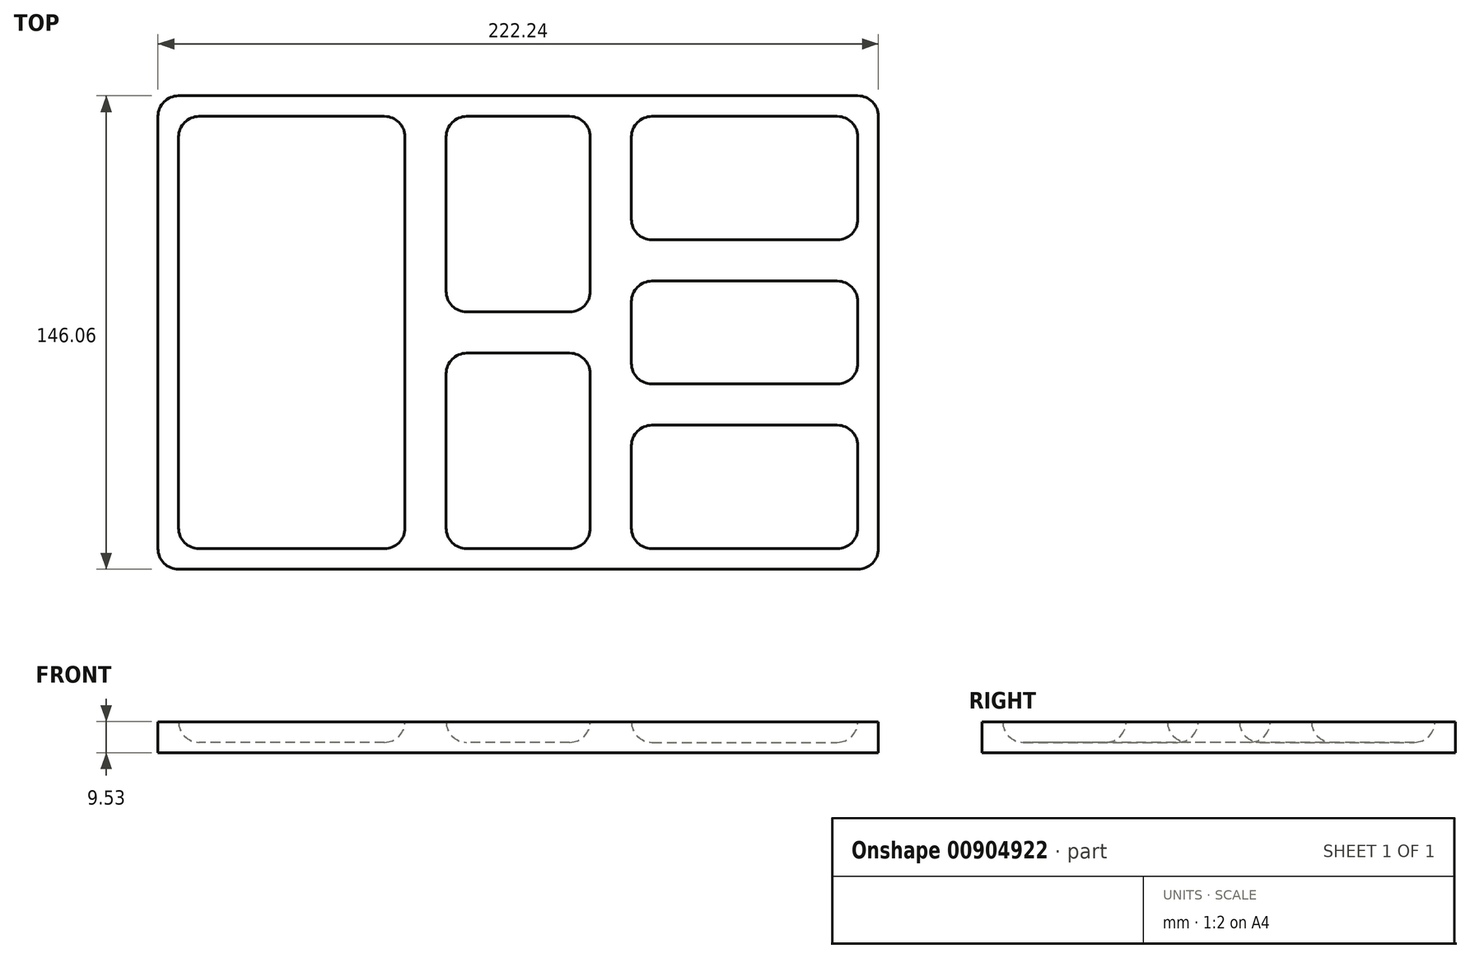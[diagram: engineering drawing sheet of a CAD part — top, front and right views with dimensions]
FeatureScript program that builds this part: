
annotation { "Feature Type Name" : "Feature", "Feature Type Description" : "" }
export const myFeature = defineFeature(function(context is Context, id is Id, definition is map)
    precondition{}
    {
        {
            var Q0;
            Q0=qCreatedBy(makeId("Top.planeOp"),FACE);
            var sketch = newSketch(context, id + "F0", { "sketchPlane" : qUnion([Q0])});
            skLineSegment(sketch, "E0.bottom", {"start": v(111.12, 73.03) * mm, "end": v(-111.13, 73.03) * mm});
            skLineSegment(sketch, "E0.top", {"start": v(111.13, -73.03) * mm, "end": v(-111.12, -73.03) * mm});
            skLineSegment(sketch, "E0.left", {"start": v(111.12, 73.03) * mm, "end": v(111.13, -73.03) * mm});
            skLineSegment(sketch, "E0.right", {"start": v(-111.13, 73.03) * mm, "end": v(-111.12, -73.03) * mm});
            skPoint(sketch, "E0.middle", {"position": v(0, 0) * mm});
            skSolve(sketch);
        }
        {
            var Q0;
            Q0 = qSketchRegion(id + "F0", true);
            extrude(context, id + "F1", {"entities" : qUnion([Q0]), "depth" : 9.52 * mm, "offsetDistance" : 25.4 * mm});
        }
        {
            var Q0;
            Q0=makeQuery(id+"F1.opExtrude","CAP_FACE",FACE,{"disambiguationData":[OSD([sQuery(id+"F0.wireOp",EDGE,"E0.bottom"),sQuery(id+"F0.wireOp",EDGE,"E0.top"),sQuery(id+"F0.wireOp",EDGE,"E0.left"),sQuery(id+"F0.wireOp",EDGE,"E0.right")])],"isStart":false});
            var sketch = newSketch(context, id + "F2", { "sketchPlane" : qUnion([Q0])});
            skLineSegment(sketch, "E1.bottom", {"start": v(104.78, 66.68) * mm, "end": v(34.93, 66.68) * mm});
            skLineSegment(sketch, "E1.top", {"start": v(104.78, -66.68) * mm, "end": v(34.93, -66.68) * mm});
            skLineSegment(sketch, "E1.left", {"start": v(104.78, 66.68) * mm, "end": v(104.78, 28.58) * mm});
            skLineSegment(sketch, "E1.right", {"start": v(-104.78, 66.68) * mm, "end": v(-104.78, -66.68) * mm});
            skPoint(sketch, "E1.middle", {"position": v(0, 0) * mm});
            skLineSegment(sketch, "E2", {"start": v(-104.78, 22.23) * mm, "end": v(104.78, 22.23) * mm, "construction": true});
            skLineSegment(sketch, "E3", {"start": v(-104.78, -22.23) * mm, "end": v(104.78, -22.23) * mm, "construction": true});
            skLineSegment(sketch, "E4", {"start": v(28.57, 66.68) * mm, "end": v(28.58, -66.68) * mm, "construction": true});
            skLineSegment(sketch, "E5", {"start": v(34.92, 66.68) * mm, "end": v(34.92, 28.57) * mm});
            skLineSegment(sketch, "E6", {"start": v(34.92, 28.57) * mm, "end": v(104.78, 28.58) * mm});
            skLineSegment(sketch, "E7", {"start": v(104.78, 15.88) * mm, "end": v(34.93, 15.87) * mm});
            skLineSegment(sketch, "E8", {"start": v(34.93, 15.87) * mm, "end": v(34.93, -15.88) * mm});
            skLineSegment(sketch, "E9", {"start": v(34.93, -15.88) * mm, "end": v(104.78, -15.88) * mm});
            skLineSegment(sketch, "E10", {"start": v(104.78, -28.58) * mm, "end": v(34.93, -28.58) * mm});
            skLineSegment(sketch, "E11", {"start": v(34.93, -28.58) * mm, "end": v(34.93, -66.68) * mm});
            skLineSegment(sketch, "E12", {"start": v(22.23, -66.68) * mm, "end": v(22.23, -6.35) * mm});
            skLineSegment(sketch, "E13.trimOffspring", {"start": v(22.23, 66.68) * mm, "end": v(-22.22, 66.68) * mm});
            skLineSegment(sketch, "E14.trimOffspring", {"start": v(104.78, 15.88) * mm, "end": v(104.78, -15.88) * mm});
            skLineSegment(sketch, "E15.trimOffspring", {"start": v(104.78, -28.58) * mm, "end": v(104.78, -66.68) * mm});
            skLineSegment(sketch, "E16.trimOffspring", {"start": v(22.23, -66.68) * mm, "end": v(-22.22, -66.68) * mm});
            skLineSegment(sketch, "E17", {"start": v(-28.58, 66.68) * mm, "end": v(-28.57, -66.68) * mm, "construction": true});
            skLineSegment(sketch, "E18", {"start": v(22.23, 0) * mm, "end": v(-28.58, 0) * mm, "construction": true});
            skLineSegment(sketch, "E19", {"start": v(-34.93, 66.68) * mm, "end": v(-34.92, -66.68) * mm});
            skLineSegment(sketch, "E20", {"start": v(-22.22, -66.68) * mm, "end": v(-22.23, -6.35) * mm});
            skLineSegment(sketch, "E21", {"start": v(-22.23, -6.35) * mm, "end": v(22.23, -6.35) * mm});
            skLineSegment(sketch, "E22", {"start": v(22.23, 6.35) * mm, "end": v(-22.22, 6.35) * mm});
            skLineSegment(sketch, "E23", {"start": v(-22.22, 6.35) * mm, "end": v(-22.23, 66.68) * mm});
            skLineSegment(sketch, "E24.trimOffspring", {"start": v(-34.92, 66.68) * mm, "end": v(-104.78, 66.68) * mm});
            skLineSegment(sketch, "E25.trimOffspring", {"start": v(-34.92, -66.68) * mm, "end": v(-104.78, -66.68) * mm});
            skLineSegment(sketch, "E26.trimOffspring", {"start": v(22.23, 6.35) * mm, "end": v(22.22, 66.68) * mm});
            skSolve(sketch);
        }
        {
            var Q0;
            Q0 = qSketchRegion(id + "F2", true);
            extrude(context, id + "F3", {"entities" : qUnion([Q0]), "operationType" : NewBodyOperationType.REMOVE, "oppositeDirection" : true, "depth" : 6.35 * mm, "offsetDistance" : 25.4 * mm});
        }
        {
            var Q0;
            Q0=makeQuery(id+"F3.boolean.opBoolean","COPY",EDGE,{"derivedFrom":makeQuery(id+"F3.opExtrude","SWEPT_EDGE",EDGE,{"disambiguationData":[OSD([sQuery(id+"F2.wireOp",EDGE,"E1.right"),sQuery(id+"F2.wireOp",EDGE,"E13.trimOffspring")])]})});
            var Q1;
            Q1=makeQuery(id+"F3.boolean.opBoolean","COPY",EDGE,{"derivedFrom":makeQuery(id+"F3.opExtrude","SWEPT_EDGE",EDGE,{"disambiguationData":[OSD([sQuery(id+"F2.wireOp",EDGE,"E12"),sQuery(id+"F2.wireOp",EDGE,"E13.trimOffspring")])]})});
            var Q2;
            Q2=makeQuery(id+"F3.boolean.opBoolean","COPY",EDGE,{"derivedFrom":makeQuery(id+"F3.opExtrude","SWEPT_EDGE",EDGE,{"disambiguationData":[OSD([sQuery(id+"F2.wireOp",EDGE,"E1.right"),sQuery(id+"F2.wireOp",EDGE,"E16.trimOffspring")])]})});
            var Q3;
            Q3=makeQuery(id+"F3.boolean.opBoolean","COPY",EDGE,{"derivedFrom":makeQuery(id+"F3.opExtrude","SWEPT_EDGE",EDGE,{"disambiguationData":[OSD([sQuery(id+"F2.wireOp",EDGE,"E12"),sQuery(id+"F2.wireOp",EDGE,"E16.trimOffspring")])]})});
            var Q4;
            Q4=makeQuery(id+"F3.boolean.opBoolean","COPY",EDGE,{"derivedFrom":makeQuery(id+"F3.opExtrude","SWEPT_EDGE",EDGE,{"disambiguationData":[OSD([sQuery(id+"F2.wireOp",EDGE,"E1.bottom"),sQuery(id+"F2.wireOp",EDGE,"E5")])]})});
            var Q5;
            Q5=makeQuery(id+"F3.boolean.opBoolean","COPY",EDGE,{"derivedFrom":makeQuery(id+"F3.opExtrude","SWEPT_EDGE",EDGE,{"disambiguationData":[OSD([sQuery(id+"F2.wireOp",EDGE,"E1.bottom"),sQuery(id+"F2.wireOp",EDGE,"E1.left")])]})});
            var Q6;
            Q6=makeQuery(id+"F3.boolean.opBoolean","COPY",EDGE,{"derivedFrom":makeQuery(id+"F3.opExtrude","SWEPT_EDGE",EDGE,{"disambiguationData":[OSD([sQuery(id+"F2.wireOp",EDGE,"E5"),sQuery(id+"F2.wireOp",EDGE,"E6")])]})});
            var Q7;
            Q7=makeQuery(id+"F3.boolean.opBoolean","COPY",EDGE,{"derivedFrom":makeQuery(id+"F3.opExtrude","SWEPT_EDGE",EDGE,{"disambiguationData":[OSD([sQuery(id+"F2.wireOp",EDGE,"E1.left"),sQuery(id+"F2.wireOp",EDGE,"E6")])]})});
            var Q8;
            Q8=makeQuery(id+"F3.boolean.opBoolean","COPY",EDGE,{"derivedFrom":makeQuery(id+"F3.opExtrude","SWEPT_EDGE",EDGE,{"disambiguationData":[OSD([sQuery(id+"F2.wireOp",EDGE,"E9"),sQuery(id+"F2.wireOp",EDGE,"E14.trimOffspring")])]})});
            var Q9;
            Q9=makeQuery(id+"F3.boolean.opBoolean","COPY",EDGE,{"derivedFrom":makeQuery(id+"F3.opExtrude","SWEPT_EDGE",EDGE,{"disambiguationData":[OSD([sQuery(id+"F2.wireOp",EDGE,"E7"),sQuery(id+"F2.wireOp",EDGE,"E8")])]})});
            var Q10;
            Q10=makeQuery(id+"F3.boolean.opBoolean","COPY",EDGE,{"derivedFrom":makeQuery(id+"F3.opExtrude","SWEPT_EDGE",EDGE,{"disambiguationData":[OSD([sQuery(id+"F2.wireOp",EDGE,"E8"),sQuery(id+"F2.wireOp",EDGE,"E9")])]})});
            var Q11;
            Q11=makeQuery(id+"F3.boolean.opBoolean","COPY",EDGE,{"derivedFrom":makeQuery(id+"F3.opExtrude","SWEPT_EDGE",EDGE,{"disambiguationData":[OSD([sQuery(id+"F2.wireOp",EDGE,"E7"),sQuery(id+"F2.wireOp",EDGE,"E14.trimOffspring")])]})});
            var Q12;
            Q12=makeQuery(id+"F3.boolean.opBoolean","COPY",EDGE,{"derivedFrom":makeQuery(id+"F3.opExtrude","SWEPT_EDGE",EDGE,{"disambiguationData":[OSD([sQuery(id+"F2.wireOp",EDGE,"E1.top"),sQuery(id+"F2.wireOp",EDGE,"E11")])]})});
            var Q13;
            Q13=makeQuery(id+"F3.boolean.opBoolean","COPY",EDGE,{"derivedFrom":makeQuery(id+"F3.opExtrude","SWEPT_EDGE",EDGE,{"disambiguationData":[OSD([sQuery(id+"F2.wireOp",EDGE,"E1.top"),sQuery(id+"F2.wireOp",EDGE,"E15.trimOffspring")])]})});
            var Q14;
            Q14=makeQuery(id+"F3.boolean.opBoolean","COPY",EDGE,{"derivedFrom":makeQuery(id+"F3.opExtrude","SWEPT_EDGE",EDGE,{"disambiguationData":[OSD([sQuery(id+"F2.wireOp",EDGE,"E10"),sQuery(id+"F2.wireOp",EDGE,"E15.trimOffspring")])]})});
            var Q15;
            Q15=makeQuery(id+"F3.boolean.opBoolean","COPY",EDGE,{"derivedFrom":makeQuery(id+"F3.opExtrude","SWEPT_EDGE",EDGE,{"disambiguationData":[OSD([sQuery(id+"F2.wireOp",EDGE,"E10"),sQuery(id+"F2.wireOp",EDGE,"E11")])]})});
            var Q16;
            Q16=makeQuery(id+"F3.boolean.opBoolean","COPY",EDGE,{"derivedFrom":makeQuery(id+"F3.opExtrude","SWEPT_EDGE",EDGE,{"disambiguationData":[OSD([sQuery(id+"F2.wireOp",EDGE,"E19"),sQuery(id+"F2.wireOp",EDGE,"E24.trimOffspring")])]})});
            var Q17;
            Q17=makeQuery(id+"F3.boolean.opBoolean","COPY",EDGE,{"derivedFrom":makeQuery(id+"F3.opExtrude","SWEPT_EDGE",EDGE,{"disambiguationData":[OSD([sQuery(id+"F2.wireOp",EDGE,"E19"),sQuery(id+"F2.wireOp",EDGE,"E25.trimOffspring")])]})});
            var Q18;
            Q18=makeQuery(id+"F3.boolean.opBoolean","COPY",EDGE,{"derivedFrom":makeQuery(id+"F3.opExtrude","SWEPT_EDGE",EDGE,{"disambiguationData":[OSD([sQuery(id+"F2.wireOp",EDGE,"E20"),sQuery(id+"F2.wireOp",EDGE,"E21")])]})});
            var Q19;
            Q19=makeQuery(id+"F3.boolean.opBoolean","COPY",EDGE,{"derivedFrom":makeQuery(id+"F3.opExtrude","SWEPT_EDGE",EDGE,{"disambiguationData":[OSD([sQuery(id+"F2.wireOp",EDGE,"E22"),sQuery(id+"F2.wireOp",EDGE,"E23")])]})});
            var Q20;
            Q20=makeQuery(id+"F3.boolean.opBoolean","COPY",EDGE,{"derivedFrom":makeQuery(id+"F3.opExtrude","SWEPT_EDGE",EDGE,{"disambiguationData":[OSD([sQuery(id+"F2.wireOp",EDGE,"E22"),sQuery(id+"F2.wireOp",EDGE,"E26.trimOffspring")])]})});
            fillet(context, id + "F4", {"entities" : qUnion([Q0, Q1, Q2, Q3, Q4, Q5, Q6, Q7, Q8, Q9, Q10, Q11, Q12, Q13, Q14, Q15, Q16, Q17, Q18, Q19, Q20]), "radius" : 6.35 * mm, "tangentPropagation" : true, "allowEdgeOverflow" : false});
        }
        {
            var Q0;
            Q0=makeQuery(id+"F1.opExtrude","SWEPT_EDGE",EDGE,{"disambiguationData":[OSD([sQuery(id+"F0.wireOp",EDGE,"E0.bottom"),sQuery(id+"F0.wireOp",EDGE,"E0.right")])]});
            var Q1;
            Q1=makeQuery(id+"F1.opExtrude","SWEPT_EDGE",EDGE,{"disambiguationData":[OSD([sQuery(id+"F0.wireOp",EDGE,"E0.top"),sQuery(id+"F0.wireOp",EDGE,"E0.right")])]});
            var Q2;
            Q2=makeQuery(id+"F1.opExtrude","SWEPT_EDGE",EDGE,{"disambiguationData":[OSD([sQuery(id+"F0.wireOp",EDGE,"E0.top"),sQuery(id+"F0.wireOp",EDGE,"E0.left")])]});
            var Q3;
            Q3=makeQuery(id+"F1.opExtrude","SWEPT_EDGE",EDGE,{"disambiguationData":[OSD([sQuery(id+"F0.wireOp",EDGE,"E0.bottom"),sQuery(id+"F0.wireOp",EDGE,"E0.left")])]});
            fillet(context, id + "F5", {"entities" : qUnion([Q0, Q1, Q2, Q3]), "radius" : 6.35 * mm, "tangentPropagation" : true, "allowEdgeOverflow" : false});
        }
        {
            var Q0;
            Q0=makeQuery(id+"F3.boolean.opBoolean","COPY",FACE,{"derivedFrom":makeQuery(id+"F3.opExtrude","CAP_FACE",FACE,{"disambiguationData":[OSD([sQuery(id+"F2.wireOp",EDGE,"E1.right"),sQuery(id+"F2.wireOp",EDGE,"E19"),sQuery(id+"F2.wireOp",EDGE,"E24.trimOffspring"),sQuery(id+"F2.wireOp",EDGE,"E25.trimOffspring")])],"isStart":false})});
            var Q1;
            Q1=makeQuery(id+"F3.boolean.opBoolean","COPY",FACE,{"derivedFrom":makeQuery(id+"F3.opExtrude","CAP_FACE",FACE,{"disambiguationData":[OSD([sQuery(id+"F2.wireOp",EDGE,"E13.trimOffspring"),sQuery(id+"F2.wireOp",EDGE,"E22"),sQuery(id+"F2.wireOp",EDGE,"E23"),sQuery(id+"F2.wireOp",EDGE,"E26.trimOffspring")])],"isStart":false})});
            var Q2;
            Q2=makeQuery(id+"F3.boolean.opBoolean","COPY",FACE,{"derivedFrom":makeQuery(id+"F3.opExtrude","CAP_FACE",FACE,{"disambiguationData":[OSD([sQuery(id+"F2.wireOp",EDGE,"E1.bottom"),sQuery(id+"F2.wireOp",EDGE,"E1.left"),sQuery(id+"F2.wireOp",EDGE,"E5"),sQuery(id+"F2.wireOp",EDGE,"E6")])],"isStart":false})});
            var Q3;
            Q3=makeQuery(id+"F3.boolean.opBoolean","COPY",FACE,{"derivedFrom":makeQuery(id+"F3.opExtrude","CAP_FACE",FACE,{"disambiguationData":[OSD([sQuery(id+"F2.wireOp",EDGE,"E7"),sQuery(id+"F2.wireOp",EDGE,"E8"),sQuery(id+"F2.wireOp",EDGE,"E9"),sQuery(id+"F2.wireOp",EDGE,"E14.trimOffspring")])],"isStart":false})});
            var Q4;
            Q4=makeQuery(id+"F3.boolean.opBoolean","COPY",FACE,{"derivedFrom":makeQuery(id+"F3.opExtrude","CAP_FACE",FACE,{"disambiguationData":[OSD([sQuery(id+"F2.wireOp",EDGE,"E1.top"),sQuery(id+"F2.wireOp",EDGE,"E10"),sQuery(id+"F2.wireOp",EDGE,"E11"),sQuery(id+"F2.wireOp",EDGE,"E15.trimOffspring")])],"isStart":false})});
            var Q5;
            Q5=makeQuery(id+"F3.boolean.opBoolean","COPY",FACE,{"derivedFrom":makeQuery(id+"F3.opExtrude","CAP_FACE",FACE,{"disambiguationData":[OSD([sQuery(id+"F2.wireOp",EDGE,"E12"),sQuery(id+"F2.wireOp",EDGE,"E16.trimOffspring"),sQuery(id+"F2.wireOp",EDGE,"E20"),sQuery(id+"F2.wireOp",EDGE,"E21")])],"isStart":false})});
            fillet(context, id + "F6", {"entities" : qUnion([Q0, Q1, Q2, Q3, Q4, Q5]), "radius" : 6.35 * mm, "tangentPropagation" : true, "allowEdgeOverflow" : false});
        }
    });
